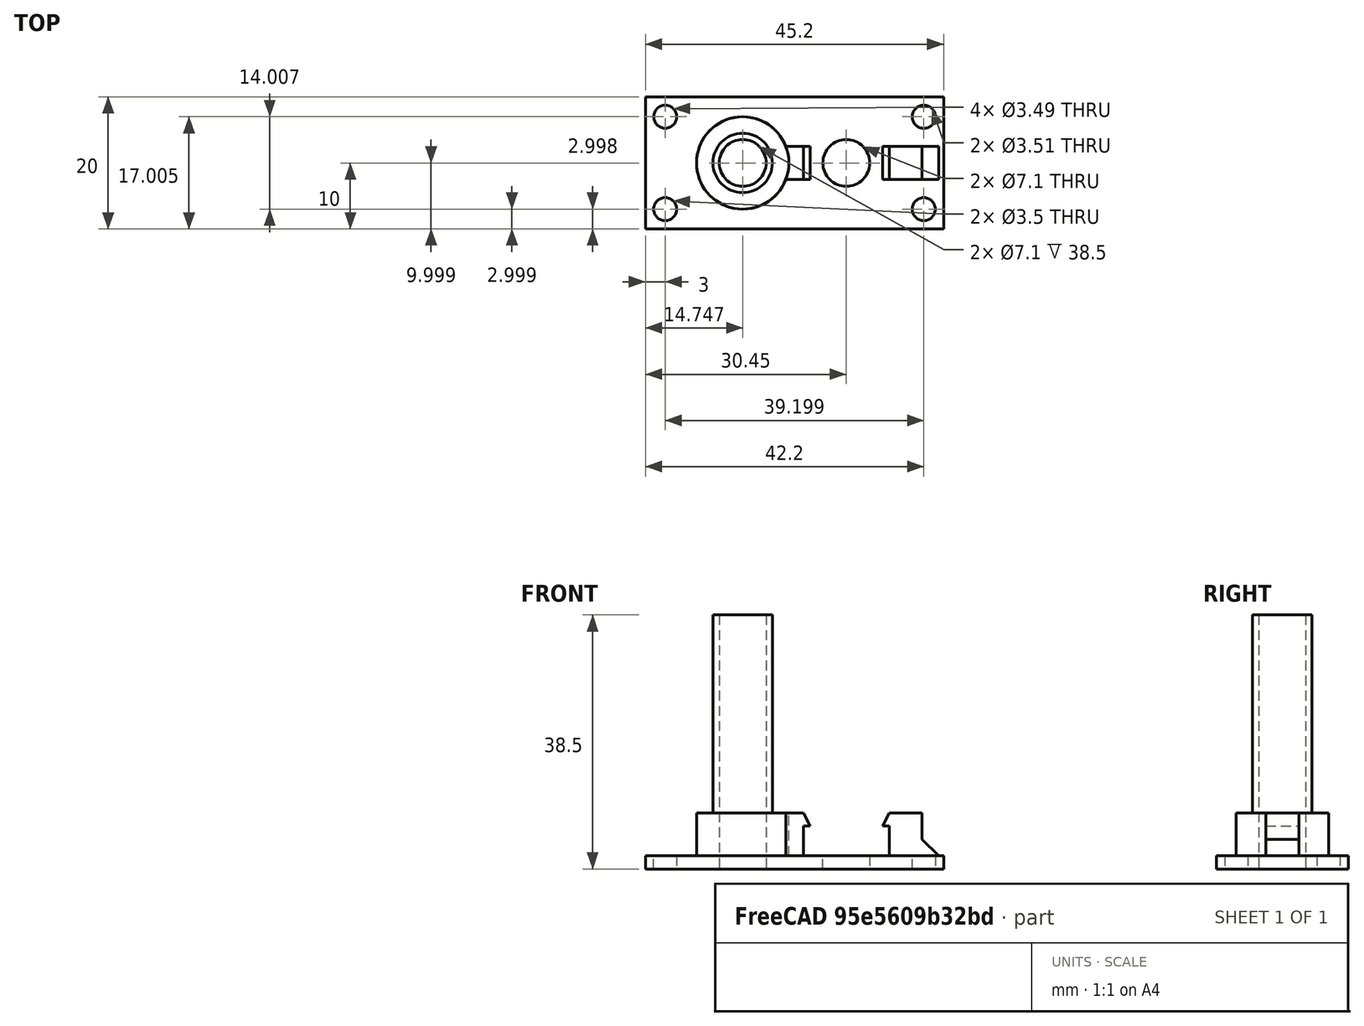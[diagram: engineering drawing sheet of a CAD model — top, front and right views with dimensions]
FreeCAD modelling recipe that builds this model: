
FCSTD DOCUMENT  (FreeCAD 0.17R13522 (Git))
Label: base_media_con_soportes_v2
License: CreativeCommons Attribution-ShareAlike
LicenseURL: http://creativecommons.org/licenses/by-sa/4.0/
objects: Part::Part2DObjectPython×11, Part::Extrusion×11, Part::Cut×10, Part::Fuse×6, Part::Feature×3, Part::Box×1, Part::MultiFuse×1, Part::Chamfer×1
note: 44 computed .brp shape members not serialized (recipe doc carries the construction recipe); baked Part::Feature solids carry a one-line shape summary decoded from their .brp

FEATURE [Part::Box] Box  label="placa base"
  AttacherType = Attacher::AttachEngine3D
  Height = 2
  Length = 45.2
  Width = 20
FEATURE [Part::Part2DObjectPython] Circle  label="taladro inferior izquierdo"  # Draft 2D object (typed FeaturePython)
  FirstAngle = 0
  LastAngle = 0
  MakeFace = false
  Placement = pos=(3,2.99873,2) rot=(0,0,1;3.14159rad)
  Radius = 1.74945
FEATURE [Part::Part2DObjectPython] Circle001  label="taladro inferior derecho"  # Draft 2D object (typed FeaturePython)
  FirstAngle = 0
  LastAngle = 0
  MakeFace = false
  Placement = pos=(42.1991,2.99781,2) rot=(0,0,1;3.14159rad)
  Radius = 1.7464
FEATURE [Part::Part2DObjectPython] Circle002  label="taladro superior derecho"  # Draft 2D object (typed FeaturePython)
  FirstAngle = 0
  LastAngle = 0
  MakeFace = false
  Placement = pos=(42.2,17.005,2) rot=(0,0,1;3.14159rad)
  Radius = 1.75369
FEATURE [Part::Part2DObjectPython] Circle003  label="taladro superior izquierdo"  # Draft 2D object (typed FeaturePython)
  FirstAngle = 0
  LastAngle = 0
  MakeFace = false
  Placement = pos=(3,17.005,2) rot=(0,0,1;3.14159rad)
  Radius = 1.74699
FEATURE [Part::Extrusion] Extrude
  Base = -> Circle003
  Dir = (0,0,1)
  DirMode = 2
  FaceMakerClass = Part::FaceMakerBullseye
  LengthFwd = 10
  LengthRev = 0
  Placement = pos=(0,0,-5) rot=(0,0,1;0rad)
  Solid = true
  Symmetric = false
FEATURE [Part::Extrusion] Extrude001
  Base = -> Circle
  Dir = (0,0,1)
  DirMode = 2
  FaceMakerClass = Part::FaceMakerBullseye
  LengthFwd = 10
  LengthRev = 0
  Placement = pos=(0,0,-5) rot=(0,0,1;0rad)
  Solid = true
  Symmetric = false
FEATURE [Part::Extrusion] Extrude002
  Base = -> Circle001
  Dir = (0,0,1)
  DirMode = 2
  FaceMakerClass = Part::FaceMakerBullseye
  LengthFwd = 10
  LengthRev = 0
  Placement = pos=(0,0,-5) rot=(0,0,1;0rad)
  Solid = true
  Symmetric = false
FEATURE [Part::Extrusion] Extrude003
  Base = -> Circle002
  Dir = (0,0,1)
  DirMode = 2
  FaceMakerClass = Part::FaceMakerBullseye
  LengthFwd = 10
  LengthRev = 0
  Placement = pos=(0,0,-5) rot=(0,0,1;0rad)
  Solid = true
  Symmetric = false
FEATURE [Part::Cut] Cut
  Base = -> Box
  Refine = true
  Tool = -> Extrude001
FEATURE [Part::Cut] Cut001
  Base = -> Cut
  Refine = true
  Tool = -> Extrude
FEATURE [Part::Cut] Cut002
  Base = -> Cut001
  Refine = true
  Tool = -> Extrude002
FEATURE [Part::Cut] Cut003  label="base con taladros en esquina"
  Base = -> Cut002
  Refine = true
  Tool = -> Extrude003
FEATURE [Part::Part2DObjectPython] Circle004  # Draft 2D object (typed FeaturePython)
  FirstAngle = 0
  LastAngle = 0
  MakeFace = false
  Placement = pos=(30.45,10,2) rot=(0,0,1;3.14159rad)
  Radius = 3.55
FEATURE [Part::Extrusion] Extrude004
  Base = -> Circle004
  Dir = (0,0,1)
  DirMode = 2
  FaceMakerClass = Part::FaceMakerBullseye
  LengthFwd = 10
  LengthRev = 0
  Placement = pos=(0,0,-4) rot=(0,0,1;0rad)
  Solid = true
  Symmetric = false
FEATURE [Part::Cut] Cut004  label="base con agujeros"
  Base = -> Cut003
  Refine = true
  Tool = -> Extrude004
FEATURE [Part::Feature] Cut004_solid001001  label="base con agujeros (Solid)002"
  shape: bbox 45.2 x 20 x 2 mm, 11 faces (baked)
FEATURE [Part::Part2DObjectPython] Circle005  # Draft 2D object (typed FeaturePython)
  FirstAngle = 0
  LastAngle = 0
  MakeFace = false
  Placement = pos=(14.7474,9.99931,2) rot=(0,0,1;0rad)
  Radius = 3.55
FEATURE [Part::Part2DObjectPython] Circle006  # Draft 2D object (typed FeaturePython)
  FirstAngle = 0
  LastAngle = 0
  MakeFace = false
  Placement = pos=(14.7474,9.99931,2) rot=(0,0,1;0rad)
  Radius = 4.5
  Support = -> [Cut004_solid001001]
FEATURE [Part::Part2DObjectPython] Circle007  # Draft 2D object (typed FeaturePython)
  FirstAngle = 0
  LastAngle = 0
  MakeFace = false
  Placement = pos=(14.7474,9.99931,2) rot=(0,0,1;0rad)
  Radius = 7
FEATURE [Part::Extrusion] Extrude005
  Base = -> Circle005
  Dir = (0,0,1)
  DirMode = 2
  FaceMakerClass = Part::FaceMakerBullseye
  LengthFwd = 50
  LengthRev = 0
  Solid = true
  Symmetric = false
FEATURE [Part::Extrusion] Extrude006
  Base = -> Circle006
  Dir = (0,0,1)
  DirMode = 2
  FaceMakerClass = Part::FaceMakerBullseye
  LengthFwd = 36.5
  LengthRev = 0
  Solid = true
  Symmetric = false
FEATURE [Part::Extrusion] Extrude007
  Base = -> Circle007
  Dir = (0,0,1)
  DirMode = 2
  FaceMakerClass = Part::FaceMakerBullseye
  LengthFwd = 6.5
  LengthRev = 0
  Solid = true
  Symmetric = false
FEATURE [Part::MultiFuse] Fusion
  Refine = true
  Shapes = -> [Cut004_solid001001,Extrude007,Extrude006]
FEATURE [Part::Cut] Cut005
  Base = -> Fusion
  Refine = true
  Tool = -> Extrude005
FEATURE [Part::Part2DObjectPython] Circle008  # Draft 2D object (typed FeaturePython)
  FirstAngle = 0
  LastAngle = 0
  MakeFace = false
  Placement = pos=(14.7474,9.99931,2) rot=(0,0,1;0rad)
  Radius = 3.55
FEATURE [Part::Extrusion] Extrude008
  Base = -> Circle008
  Dir = (0,0,1)
  DirMode = 2
  FaceMakerClass = Part::FaceMakerBullseye
  LengthFwd = 50
  LengthRev = 0
  Placement = pos=(0,0,-7) rot=(0,0,1;0rad)
  Solid = true
  Symmetric = false
FEATURE [Part::Cut] Cut006
  Base = -> Cut005
  Refine = true
  Tool = -> Extrude008
FEATURE [Part::Feature] Clone002
  Placement = pos=(22.6,10,-1.5) rot=(0,0,1;0rad)
  shape: bbox 6 x 5 x 8 mm, 10 faces (baked)
FEATURE [Part::Feature] Clone001001  label="Clone003"
  Placement = pos=(38.3,10,9.927e-05) rot=(0,0,1;0rad)
  shape: bbox 6 x 5 x 8 mm, 10 faces (baked)
FEATURE [Part::Fuse] Fusion001
  Base = -> Extrude007
  Refine = true
  Tool = -> Clone002
FEATURE [Part::Cut] Cut007
  Base = -> Cut004
  Refine = true
  Tool = -> Extrude008
FEATURE [Part::Fuse] Fusion002
  Base = -> Clone001001
  Refine = true
  Tool = -> Cut007
FEATURE [Part::Chamfer] Chamfer
  Base = -> Fusion002
  Edges = 1 edges r=2.5: [Edge24]
FEATURE [Part::Cut] Cut008
  Base = -> Fusion
  Refine = true
  Tool = -> Extrude005
FEATURE [Part::Fuse] Fusion003
  Base = -> Fusion001
  Refine = true
  Tool = -> Chamfer
FEATURE [Part::Fuse] Fusion004
  Base = -> Cut008
  Refine = true
  Tool = -> Fusion003
FEATURE [Part::Cut] Cut009
  Base = -> Fusion004
  Refine = true
  Tool = -> Extrude008
FEATURE [Part::Part2DObjectPython] Rectangle  # Draft 2D object (typed FeaturePython)
  ChamferSize = 0
  Columns = 1
  FilletRadius = 0
  Height = 1.80868
  Length = 0.123222
  MakeFace = true
  Placement = pos=(23.8348,7.5,6.49553) rot=(1,0,0;1.5708rad)
  Rows = 1
FEATURE [Part::Extrusion] Extrude009
  Base = -> Rectangle
  Dir = (0,-1,0)
  DirMode = 2
  FaceMakerClass = Part::FaceMakerBullseye
  LengthFwd = 5
  LengthRev = 0
  Placement = pos=(0,5,0) rot=(0,0,1;0rad)
  Solid = false
  Symmetric = false
FEATURE [Part::Fuse] Fusion005
  Base = -> Cut009
  Refine = true
  Tool = -> Extrude009
FEATURE [Part::Part2DObjectPython] Rectangle001  # Draft 2D object (typed FeaturePython)
  ChamferSize = 0
  Columns = 1
  FilletRadius = 0
  Height = 1.81025
  Length = 0.139714
  MakeFace = true
  Placement = pos=(36.942,7.5,6.49563) rot=(1,0,0;1.5708rad)
  Rows = 1
FEATURE [Part::Extrusion] Extrude010
  Base = -> Rectangle001
  Dir = (0,-1,0)
  DirMode = 2
  FaceMakerClass = Part::FaceMakerBullseye
  LengthFwd = 5
  LengthRev = 0
  Placement = pos=(0,5,0) rot=(0,0,1;0rad)
  Solid = false
  Symmetric = false
FEATURE [Part::Fuse] Fusion006
  Base = -> Fusion005
  Refine = true
  Tool = -> Extrude010
